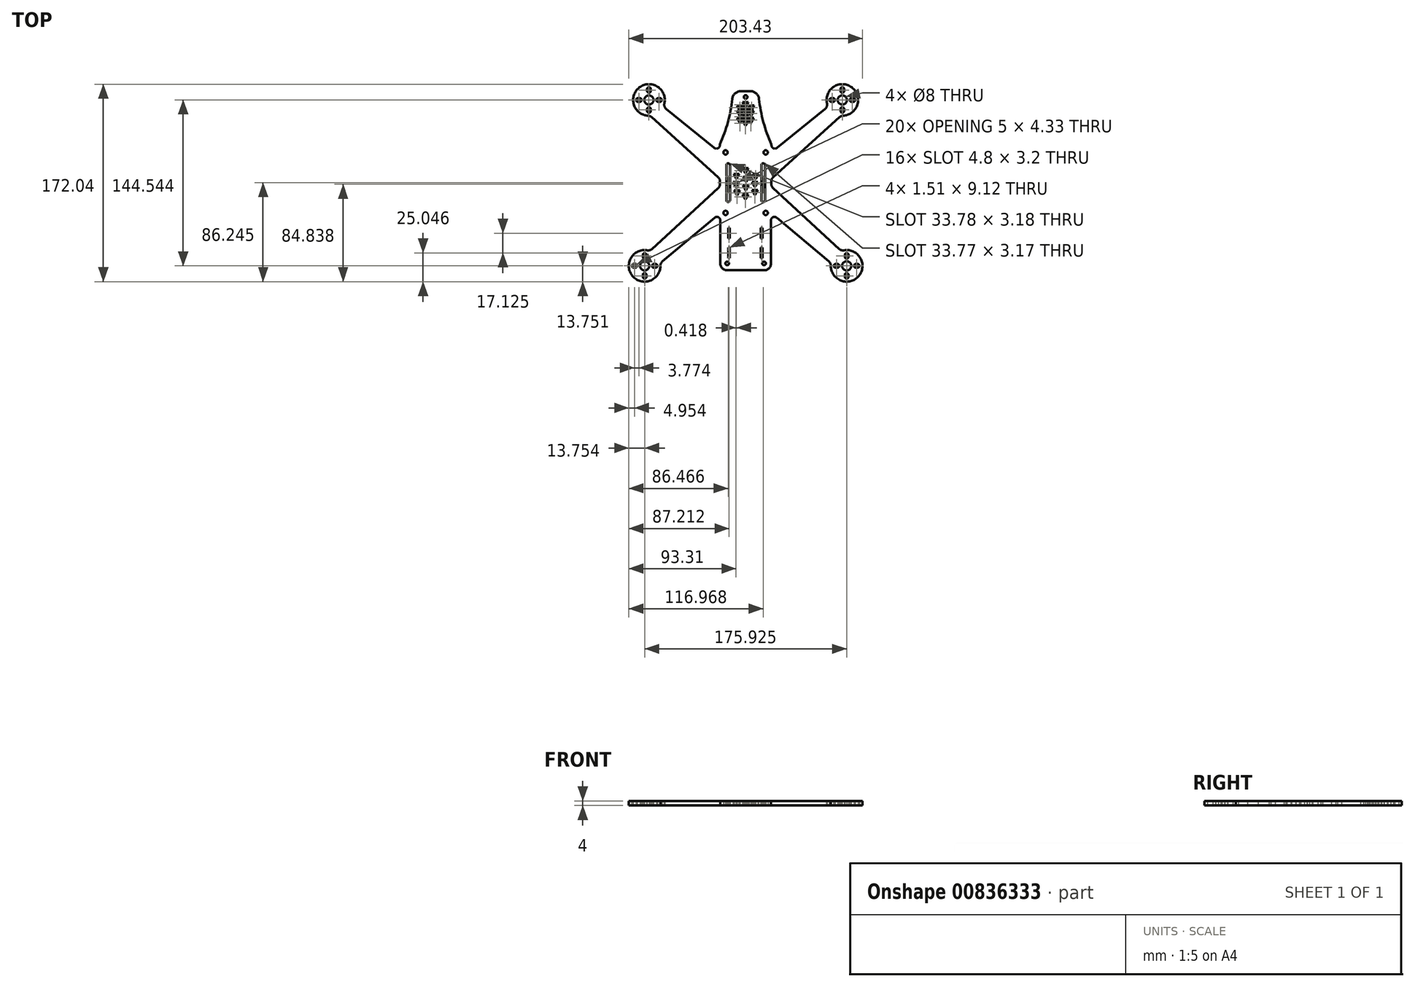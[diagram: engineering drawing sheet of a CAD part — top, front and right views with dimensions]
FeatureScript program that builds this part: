
annotation { "Feature Type Name" : "Feature", "Feature Type Description" : "" }
export const myFeature = defineFeature(function(context is Context, id is Id, definition is map)
    precondition{}
    {
        {
            var Q0;
            Q0=qCreatedBy(makeId("Top.planeOp"),FACE);
            var sketch = newSketch(context, id + "F0", { "sketchPlane" : qUnion([Q0])});
            skLineSegment(sketch, "E0.MirrorCS", {"start": v(-18.92, -69.92) * mm, "end": v(38.48, -122.77) * mm});
            skLineSegment(sketch, "E1.MirrorCS", {"start": v(-15.91, -95.57) * mm, "end": v(29.51, -133.68) * mm});
            skLineSegment(sketch, "E2.trimOffspring", {"start": v(-20.53, -63.92) * mm, "end": v(-20.53, -66.23) * mm});
            skLineSegment(sketch, "E3.MirrorCS", {"start": v(-18.88, -60.23) * mm, "end": v(38.94, -8.04) * mm});
            skLineSegment(sketch, "E4.MirrorCS", {"start": v(-15.53, -34.75) * mm, "end": v(26.13, -1.02) * mm});
            skArc(sketch, "E5.MirrorCS", {"start": v(-38.56, 7.2) * mm, "mid": v(-38.56, 7.2) * mm, "end": v(-38.56, 7.2) * mm});
            skLineSegment(sketch, "E6", {"start": v(-42.91, 14.57) * mm, "end": v(-38.56, 14.57) * mm});
            skLineSegment(sketch, "E7", {"start": v(-20.41, -31.7) * mm, "end": v(-20.41, -38.7) * mm});
            skLineSegment(sketch, "E8", {"start": v(-20.41, -32.42) * mm, "end": v(-20.41, -31.7) * mm});
            skArc(sketch, "E9", {"start": v(-31.23, 7.96) * mm, "mid": v(-27.44, -12.31) * mm, "end": v(-20.41, -31.7) * mm});
            skArc(sketch, "E10.filletArc", {"start": v(-31.23, 7.96) * mm, "mid": v(-33.63, 12.68) * mm, "end": v(-38.56, 14.57) * mm});
            skPoint(sketch, "E11.start.orphan", {"position": v(-47.26, 14.57) * mm});
            skLineSegment(sketch, "E12.MirrorCS", {"start": v(-42.91, 14.57) * mm, "end": v(-47.26, 14.57) * mm});
            skPoint(sketch, "E13.MirrorP", {"position": v(-47.26, 7.2) * mm});
            skPoint(sketch, "E14.MirrorP", {"position": v(-38.56, 14.57) * mm});
            skCircle(sketch, "E15", {"center": v(-42.91, 9.57) * mm, "radius": 1.59 * mm});
            skArc(sketch, "E16", {"start": v(31.3, -137.53) * mm, "mid": v(55.55, -146.44) * mm, "end": v(42.72, -124.02) * mm});
            skArc(sketch, "E17", {"start": v(42.02, -6.75) * mm, "mid": v(49.57, 17.94) * mm, "end": v(27.86, 3.96) * mm});
            skLineSegment(sketch, "E18.MirrorCS", {"start": v(33.27, 8.58) * mm, "end": v(31.67, 8.58) * mm});
            skArc(sketch, "E19.MirrorCS", {"start": v(33.27, 8.58) * mm, "mid": v(34.87, 6.98) * mm, "end": v(33.27, 5.38) * mm});
            skArc(sketch, "E20.MirrorCS", {"start": v(31.67, 5.38) * mm, "mid": v(30.07, 6.98) * mm, "end": v(31.67, 8.58) * mm});
            skArc(sketch, "E21.MirrorCS", {"start": v(42.87, 14.88) * mm, "mid": v(41.27, 13.28) * mm, "end": v(39.67, 14.88) * mm});
            skLineSegment(sketch, "E22.MirrorCS", {"start": v(42.87, 16.48) * mm, "end": v(42.87, 14.88) * mm});
            skLineSegment(sketch, "E23.MirrorCS", {"start": v(39.67, 16.48) * mm, "end": v(39.67, 14.88) * mm});
            skArc(sketch, "E24.MirrorCS", {"start": v(39.67, 16.48) * mm, "mid": v(41.27, 18.08) * mm, "end": v(42.87, 16.48) * mm});
            skLineSegment(sketch, "E25.MirrorCS", {"start": v(33.27, 5.38) * mm, "end": v(31.67, 5.38) * mm});
            skArc(sketch, "E26.MirrorCS", {"start": v(39.67, -0.92) * mm, "mid": v(41.27, 0.68) * mm, "end": v(42.87, -0.92) * mm});
            skLineSegment(sketch, "E27.MirrorCS", {"start": v(39.67, -2.52) * mm, "end": v(39.67, -0.92) * mm});
            skArc(sketch, "E28.MirrorCS", {"start": v(42.87, -2.52) * mm, "mid": v(41.27, -4.12) * mm, "end": v(39.67, -2.52) * mm});
            skLineSegment(sketch, "E29.MirrorCS", {"start": v(42.87, -0.92) * mm, "end": v(42.87, -2.52) * mm});
            skCircle(sketch, "E30.MirrorC", {"center": v(41.27, 6.98) * mm, "radius": 4 * mm});
            skLineSegment(sketch, "E31.MirrorCS", {"start": v(50.87, 8.58) * mm, "end": v(49.27, 8.58) * mm});
            skArc(sketch, "E32.MirrorCS", {"start": v(49.27, 5.38) * mm, "mid": v(47.67, 6.98) * mm, "end": v(49.27, 8.58) * mm});
            skLineSegment(sketch, "E33.MirrorCS", {"start": v(49.27, 5.38) * mm, "end": v(50.87, 5.38) * mm});
            skArc(sketch, "E34.MirrorCS", {"start": v(50.87, 8.58) * mm, "mid": v(52.47, 6.98) * mm, "end": v(50.87, 5.38) * mm});
            skLineSegment(sketch, "E35.MirrorCS", {"start": v(37.05, -135.97) * mm, "end": v(35.45, -135.97) * mm});
            skArc(sketch, "E36.MirrorCS", {"start": v(37.05, -135.97) * mm, "mid": v(38.65, -137.57) * mm, "end": v(37.05, -139.17) * mm});
            skArc(sketch, "E37.MirrorCS", {"start": v(35.45, -139.17) * mm, "mid": v(33.85, -137.57) * mm, "end": v(35.45, -135.97) * mm});
            skArc(sketch, "E38.MirrorCS", {"start": v(46.65, -129.67) * mm, "mid": v(45.05, -131.27) * mm, "end": v(43.45, -129.67) * mm});
            skLineSegment(sketch, "E39.MirrorCS", {"start": v(46.65, -128.07) * mm, "end": v(46.65, -129.67) * mm});
            skLineSegment(sketch, "E40.MirrorCS", {"start": v(43.45, -128.07) * mm, "end": v(43.45, -129.67) * mm});
            skArc(sketch, "E41.MirrorCS", {"start": v(43.45, -128.07) * mm, "mid": v(45.05, -126.47) * mm, "end": v(46.65, -128.07) * mm});
            skLineSegment(sketch, "E42.MirrorCS", {"start": v(37.05, -139.17) * mm, "end": v(35.45, -139.17) * mm});
            skArc(sketch, "E43.MirrorCS", {"start": v(43.45, -145.47) * mm, "mid": v(45.05, -143.87) * mm, "end": v(46.65, -145.47) * mm});
            skLineSegment(sketch, "E44.MirrorCS", {"start": v(43.45, -147.07) * mm, "end": v(43.45, -145.47) * mm});
            skArc(sketch, "E45.MirrorCS", {"start": v(46.65, -147.07) * mm, "mid": v(45.05, -148.67) * mm, "end": v(43.45, -147.07) * mm});
            skLineSegment(sketch, "E46.MirrorCS", {"start": v(46.65, -145.47) * mm, "end": v(46.65, -147.07) * mm});
            skCircle(sketch, "E47.MirrorC", {"center": v(45.05, -137.57) * mm, "radius": 4 * mm});
            skLineSegment(sketch, "E48.MirrorCS", {"start": v(54.65, -135.97) * mm, "end": v(53.05, -135.97) * mm});
            skArc(sketch, "E49.MirrorCS", {"start": v(53.05, -139.17) * mm, "mid": v(51.45, -137.57) * mm, "end": v(53.05, -135.97) * mm});
            skLineSegment(sketch, "E50.MirrorCS", {"start": v(53.05, -139.17) * mm, "end": v(54.65, -139.17) * mm});
            skArc(sketch, "E51.MirrorCS", {"start": v(54.65, -135.97) * mm, "mid": v(56.25, -137.57) * mm, "end": v(54.65, -139.17) * mm});
            skPoint(sketch, "E52.visualSharp", {"position": v(28.82, 1.16) * mm});
            skArc(sketch, "E52.filletArc", {"start": v(26.13, -1.02) * mm, "mid": v(27.7, 1.22) * mm, "end": v(27.86, 3.96) * mm});
            skPoint(sketch, "E53.visualSharp", {"position": v(40.37, -6.75) * mm});
            skArc(sketch, "E53.filletArc", {"start": v(42.02, -6.75) * mm, "mid": v(40.37, -7.13) * mm, "end": v(38.94, -8.04) * mm});
            skPoint(sketch, "E54.visualSharp", {"position": v(-20.52, -61.7) * mm});
            skArc(sketch, "E54.filletArc", {"start": v(-18.88, -60.23) * mm, "mid": v(-20.1, -61.9) * mm, "end": v(-20.53, -63.92) * mm});
            skPoint(sketch, "E55.visualSharp", {"position": v(-20.54, -68.43) * mm});
            skArc(sketch, "E55.filletArc", {"start": v(-20.53, -66.23) * mm, "mid": v(-20.12, -68.25) * mm, "end": v(-18.92, -69.92) * mm});
            skPoint(sketch, "E56.visualSharp", {"position": v(40.47, -124.6) * mm});
            skArc(sketch, "E56.filletArc", {"start": v(38.48, -122.77) * mm, "mid": v(40.45, -123.89) * mm, "end": v(42.72, -124.02) * mm});
            skPoint(sketch, "E57.visualSharp", {"position": v(31.48, -135.33) * mm});
            skArc(sketch, "E57.filletArc", {"start": v(31.3, -137.53) * mm, "mid": v(30.83, -135.4) * mm, "end": v(29.51, -133.68) * mm});
            skLineSegment(sketch, "E58.MirrorCS", {"start": v(-129.28, -128.07) * mm, "end": v(-129.28, -129.67) * mm});
            skLineSegment(sketch, "E59.MirrorCS", {"start": v(-119.1, 5.38) * mm, "end": v(-117.5, 5.38) * mm});
            skLineSegment(sketch, "E60.MirrorCS", {"start": v(-119.1, 8.58) * mm, "end": v(-117.5, 8.58) * mm});
            skArc(sketch, "E61.MirrorCS", {"start": v(-129.28, -128.07) * mm, "mid": v(-130.88, -126.47) * mm, "end": v(-132.48, -128.07) * mm});
            skLineSegment(sketch, "E62.MirrorCS", {"start": v(-136.7, 8.58) * mm, "end": v(-135.1, 8.58) * mm});
            skArc(sketch, "E63.MirrorCS", {"start": v(-119.1, 8.58) * mm, "mid": v(-120.7, 6.98) * mm, "end": v(-119.1, 5.38) * mm});
            skLineSegment(sketch, "E64.MirrorCS", {"start": v(-129.28, -147.07) * mm, "end": v(-129.28, -145.47) * mm});
            skLineSegment(sketch, "E65.MirrorCS", {"start": v(-135.1, 5.38) * mm, "end": v(-136.7, 5.38) * mm});
            skArc(sketch, "E66.MirrorCS", {"start": v(-132.48, -129.67) * mm, "mid": v(-130.88, -131.27) * mm, "end": v(-129.28, -129.67) * mm});
            skLineSegment(sketch, "E67.MirrorCS", {"start": v(-132.48, -128.07) * mm, "end": v(-132.48, -129.67) * mm});
            skArc(sketch, "E68.MirrorCS", {"start": v(-124.3, -122.77) * mm, "mid": v(-126.28, -123.89) * mm, "end": v(-128.54, -124.02) * mm});
            skLineSegment(sketch, "E69.MirrorCS", {"start": v(-132.48, -145.47) * mm, "end": v(-132.48, -147.07) * mm});
            skArc(sketch, "E70.MirrorCS", {"start": v(-117.5, 5.38) * mm, "mid": v(-115.9, 6.98) * mm, "end": v(-117.5, 8.58) * mm});
            skLineSegment(sketch, "E71.MirrorCS", {"start": v(-122.88, -135.97) * mm, "end": v(-121.28, -135.97) * mm});
            skArc(sketch, "E72.MirrorCS", {"start": v(-135.1, 5.38) * mm, "mid": v(-133.5, 6.98) * mm, "end": v(-135.1, 8.58) * mm});
            skArc(sketch, "E73.MirrorCS", {"start": v(-136.7, 8.58) * mm, "mid": v(-138.3, 6.98) * mm, "end": v(-136.7, 5.38) * mm});
            skLineSegment(sketch, "E74.MirrorCS", {"start": v(-128.7, -0.92) * mm, "end": v(-128.7, -2.52) * mm});
            skArc(sketch, "E75.MirrorCS", {"start": v(-132.48, -147.07) * mm, "mid": v(-130.88, -148.67) * mm, "end": v(-129.28, -147.07) * mm});
            skLineSegment(sketch, "E76.MirrorCS", {"start": v(-125.5, -2.52) * mm, "end": v(-125.5, -0.92) * mm});
            skArc(sketch, "E77.MirrorCS", {"start": v(-129.28, -145.47) * mm, "mid": v(-130.88, -143.87) * mm, "end": v(-132.48, -145.47) * mm});
            skArc(sketch, "E78.MirrorCS", {"start": v(-125.5, -0.92) * mm, "mid": v(-127.1, 0.68) * mm, "end": v(-128.7, -0.92) * mm});
            skArc(sketch, "E79.MirrorCS", {"start": v(-117.13, -137.53) * mm, "mid": v(-116.66, -135.4) * mm, "end": v(-115.34, -133.68) * mm});
            skArc(sketch, "E80.MirrorCS", {"start": v(-121.28, -139.17) * mm, "mid": v(-119.68, -137.57) * mm, "end": v(-121.28, -135.97) * mm});
            skLineSegment(sketch, "E81.MirrorCS", {"start": v(-122.88, -139.17) * mm, "end": v(-121.28, -139.17) * mm});
            skLineSegment(sketch, "E82.MirrorCS", {"start": v(-125.5, 16.48) * mm, "end": v(-125.5, 14.88) * mm});
            skArc(sketch, "E83.MirrorCS", {"start": v(-47.26, 7.2) * mm, "mid": v(-47.26, 7.2) * mm, "end": v(-47.26, 7.2) * mm});
            skLineSegment(sketch, "E84.MirrorCS", {"start": v(-128.7, 16.48) * mm, "end": v(-128.7, 14.88) * mm});
            skArc(sketch, "E85.MirrorCS", {"start": v(-128.7, -2.52) * mm, "mid": v(-127.1, -4.12) * mm, "end": v(-125.5, -2.52) * mm});
            skLineSegment(sketch, "E86.MirrorCS", {"start": v(-140.48, -135.97) * mm, "end": v(-138.88, -135.97) * mm});
            skArc(sketch, "E87.MirrorCS", {"start": v(-122.88, -135.97) * mm, "mid": v(-124.48, -137.57) * mm, "end": v(-122.88, -139.17) * mm});
            skArc(sketch, "E88.MirrorCS", {"start": v(-127.85, -6.75) * mm, "mid": v(-126.2, -7.13) * mm, "end": v(-124.77, -8.04) * mm});
            skArc(sketch, "E89.MirrorCS", {"start": v(-138.88, -139.17) * mm, "mid": v(-137.28, -137.57) * mm, "end": v(-138.88, -135.97) * mm});
            skArc(sketch, "E90.MirrorCS", {"start": v(-128.7, 14.88) * mm, "mid": v(-127.1, 13.28) * mm, "end": v(-125.5, 14.88) * mm});
            skCircle(sketch, "E91.MirrorC", {"center": v(-130.88, -137.57) * mm, "radius": 4 * mm});
            skArc(sketch, "E92.MirrorCS", {"start": v(-125.5, 16.48) * mm, "mid": v(-127.1, 18.08) * mm, "end": v(-128.7, 16.48) * mm});
            skCircle(sketch, "E93.MirrorC", {"center": v(-127.1, 6.98) * mm, "radius": 4 * mm});
            skArc(sketch, "E94.MirrorCS", {"start": v(-140.48, -135.97) * mm, "mid": v(-142.08, -137.57) * mm, "end": v(-140.48, -139.17) * mm});
            skLineSegment(sketch, "E95.MirrorCS", {"start": v(-138.88, -139.17) * mm, "end": v(-140.48, -139.17) * mm});
            skArc(sketch, "E96.MirrorCS", {"start": v(-111.95, -1.02) * mm, "mid": v(-113.53, 1.22) * mm, "end": v(-113.69, 3.96) * mm});
            skLineSegment(sketch, "E97.MirrorCS", {"start": v(-65.41, -32.42) * mm, "end": v(-65.41, -31.7) * mm});
            skLineSegment(sketch, "E98.MirrorCS", {"start": v(-65.3, -63.92) * mm, "end": v(-65.3, -66.23) * mm});
            skArc(sketch, "E99.MirrorCS", {"start": v(-66.95, -60.23) * mm, "mid": v(-65.74, -61.9) * mm, "end": v(-65.3, -63.92) * mm});
            skArc(sketch, "E100.MirrorCS", {"start": v(-65.3, -66.23) * mm, "mid": v(-65.71, -68.25) * mm, "end": v(-66.9, -69.92) * mm});
            skArc(sketch, "E101.MirrorCS", {"start": v(-54.6, 7.96) * mm, "mid": v(-52.2, 12.68) * mm, "end": v(-47.26, 14.57) * mm});
            skPoint(sketch, "E102.MirrorP", {"position": v(-126.3, -124.6) * mm});
            skLineSegment(sketch, "E103.MirrorCS", {"start": v(-70.3, -34.75) * mm, "end": v(-111.95, -1.02) * mm});
            skArc(sketch, "E104.MirrorCS", {"start": v(-54.6, 7.96) * mm, "mid": v(-58.39, -12.31) * mm, "end": v(-65.41, -31.7) * mm});
            skPoint(sketch, "E105.MirrorP", {"position": v(-65.3, -61.7) * mm});
            skPoint(sketch, "E106.MirrorP", {"position": v(-114.64, 1.16) * mm});
            skPoint(sketch, "E107.MirrorP", {"position": v(-117.3, -135.33) * mm});
            skPoint(sketch, "E108.MirrorP", {"position": v(-65.28, -68.43) * mm});
            skLineSegment(sketch, "E109.MirrorCS", {"start": v(-66.95, -60.23) * mm, "end": v(-124.77, -8.04) * mm});
            skArc(sketch, "E110.MirrorCS", {"start": v(-117.13, -137.53) * mm, "mid": v(-141.38, -146.44) * mm, "end": v(-128.54, -124.02) * mm});
            skArc(sketch, "E111.MirrorCS", {"start": v(-127.85, -6.75) * mm, "mid": v(-135.4, 17.94) * mm, "end": v(-113.69, 3.96) * mm});
            skLineSegment(sketch, "E112.MirrorCS", {"start": v(-69.92, -95.57) * mm, "end": v(-115.34, -133.68) * mm});
            skPoint(sketch, "E113.MirrorP", {"position": v(-126.2, -6.75) * mm});
            skLineSegment(sketch, "E114.MirrorCS", {"start": v(-66.9, -69.92) * mm, "end": v(-124.3, -122.77) * mm});
            skLineSegment(sketch, "E115", {"start": v(-64.99, -97.87) * mm, "end": v(-64.99, -135.43) * mm});
            skLineSegment(sketch, "E116", {"start": v(-58.99, -141.43) * mm, "end": v(-26.84, -141.43) * mm});
            skLineSegment(sketch, "E117", {"start": v(-20.84, -97.87) * mm, "end": v(-20.84, -135.43) * mm});
            skPoint(sketch, "E118.visualSharp", {"position": v(-64.99, -141.43) * mm});
            skArc(sketch, "E118.filletArc", {"start": v(-64.99, -135.43) * mm, "mid": v(-63.23, -139.67) * mm, "end": v(-58.99, -141.43) * mm});
            skPoint(sketch, "E119.visualSharp", {"position": v(-20.84, -141.43) * mm});
            skArc(sketch, "E119.filletArc", {"start": v(-26.84, -141.43) * mm, "mid": v(-22.6, -139.67) * mm, "end": v(-20.84, -135.43) * mm});
            skCircle(sketch, "E120", {"center": v(-26.84, -135.43) * mm, "radius": 1.59 * mm});
            skCircle(sketch, "E121", {"center": v(-58.99, -135.43) * mm, "radius": 1.59 * mm});
            skLineSegment(sketch, "E122.0", {"start": v(-40.36, -0.31) * mm, "end": v(-42.86, -4.64) * mm});
            skLineSegment(sketch, "E122.1", {"start": v(-42.86, -4.64) * mm, "end": v(-45.36, -0.31) * mm});
            skLineSegment(sketch, "E122.2", {"start": v(-45.36, -0.31) * mm, "end": v(-40.36, -0.31) * mm});
            skPoint(sketch, "E122.0.midPoint", {"position": v(-41.61, -2.48) * mm});
            skLineSegment(sketch, "E123.0", {"start": v(-45.33, -2.7) * mm, "end": v(-47.83, -7.03) * mm});
            skLineSegment(sketch, "E123.1", {"start": v(-47.83, -7.03) * mm, "end": v(-50.33, -2.7) * mm});
            skLineSegment(sketch, "E123.2", {"start": v(-50.33, -2.7) * mm, "end": v(-45.33, -2.7) * mm});
            skPoint(sketch, "E123.0.midPoint", {"position": v(-46.58, -4.87) * mm});
            skLineSegment(sketch, "E124.0", {"start": v(-40.62, -5.4) * mm, "end": v(-43.12, -9.74) * mm});
            skLineSegment(sketch, "E124.1", {"start": v(-43.12, -9.74) * mm, "end": v(-45.62, -5.4) * mm});
            skLineSegment(sketch, "E124.2", {"start": v(-45.62, -5.4) * mm, "end": v(-40.62, -5.4) * mm});
            skPoint(sketch, "E124.0.midPoint", {"position": v(-41.87, -7.57) * mm});
            skLineSegment(sketch, "E125.0", {"start": v(-35.65, -2.7) * mm, "end": v(-38.15, -7.03) * mm});
            skLineSegment(sketch, "E125.1", {"start": v(-38.15, -7.03) * mm, "end": v(-40.65, -2.7) * mm});
            skLineSegment(sketch, "E125.2", {"start": v(-40.65, -2.7) * mm, "end": v(-35.65, -2.7) * mm});
            skPoint(sketch, "E125.0.midPoint", {"position": v(-36.9, -4.87) * mm});
            skLineSegment(sketch, "E126.0", {"start": v(-35.35, 2.37) * mm, "end": v(-37.85, -1.96) * mm});
            skLineSegment(sketch, "E126.1", {"start": v(-37.85, -1.96) * mm, "end": v(-40.35, 2.37) * mm});
            skLineSegment(sketch, "E126.2", {"start": v(-40.35, 2.37) * mm, "end": v(-35.35, 2.37) * mm});
            skPoint(sketch, "E126.0.midPoint", {"position": v(-36.6, 0.2) * mm});
            skLineSegment(sketch, "E127.0", {"start": v(-40.47, 4.97) * mm, "end": v(-42.97, 0.64) * mm});
            skLineSegment(sketch, "E127.1", {"start": v(-42.97, 0.64) * mm, "end": v(-45.47, 4.97) * mm});
            skLineSegment(sketch, "E127.2", {"start": v(-45.47, 4.97) * mm, "end": v(-40.47, 4.97) * mm});
            skPoint(sketch, "E127.0.midPoint", {"position": v(-41.72, 2.8) * mm});
            skLineSegment(sketch, "E128.0", {"start": v(-45.25, 2.37) * mm, "end": v(-47.75, -1.96) * mm});
            skLineSegment(sketch, "E128.1", {"start": v(-47.75, -1.96) * mm, "end": v(-50.25, 2.37) * mm});
            skLineSegment(sketch, "E128.2", {"start": v(-50.25, 2.37) * mm, "end": v(-45.25, 2.37) * mm});
            skPoint(sketch, "E128.0.midPoint", {"position": v(-46.5, 0.2) * mm});
            skLineSegment(sketch, "E129.0", {"start": v(-35.89, -8.43) * mm, "end": v(-38.39, -12.77) * mm});
            skLineSegment(sketch, "E129.1", {"start": v(-38.39, -12.77) * mm, "end": v(-40.89, -8.43) * mm});
            skLineSegment(sketch, "E129.2", {"start": v(-40.89, -8.43) * mm, "end": v(-35.89, -8.43) * mm});
            skPoint(sketch, "E129.0.midPoint", {"position": v(-37.14, -10.6) * mm});
            skLineSegment(sketch, "E130.0", {"start": v(-45.25, -8.43) * mm, "end": v(-47.75, -12.77) * mm});
            skLineSegment(sketch, "E130.1", {"start": v(-47.75, -12.77) * mm, "end": v(-50.25, -8.43) * mm});
            skLineSegment(sketch, "E130.2", {"start": v(-50.25, -8.43) * mm, "end": v(-45.25, -8.43) * mm});
            skPoint(sketch, "E130.0.midPoint", {"position": v(-46.5, -10.6) * mm});
            skLineSegment(sketch, "E131.0", {"start": v(-40.47, -11.03) * mm, "end": v(-42.97, -15.36) * mm});
            skLineSegment(sketch, "E131.1", {"start": v(-42.97, -15.36) * mm, "end": v(-45.47, -11.03) * mm});
            skLineSegment(sketch, "E131.2", {"start": v(-45.47, -11.03) * mm, "end": v(-40.47, -11.03) * mm});
            skPoint(sketch, "E131.0.midPoint", {"position": v(-41.72, -13.2) * mm});
            skLineSegment(sketch, "E132.bottom", {"start": v(-58.17, -121.71) * mm, "end": v(-56.66, -121.71) * mm});
            skLineSegment(sketch, "E132.top", {"start": v(-58.17, -130.84) * mm, "end": v(-56.66, -130.84) * mm});
            skLineSegment(sketch, "E132.left", {"start": v(-58.17, -121.71) * mm, "end": v(-58.17, -130.84) * mm});
            skLineSegment(sketch, "E132.right", {"start": v(-56.66, -121.71) * mm, "end": v(-56.66, -130.84) * mm});
            skLineSegment(sketch, "E133.MirrorCS", {"start": v(-28.14, -121.71) * mm, "end": v(-28.14, -130.84) * mm});
            skLineSegment(sketch, "E134.MirrorCS", {"start": v(-29.65, -121.71) * mm, "end": v(-29.65, -130.84) * mm});
            skLineSegment(sketch, "E135.MirrorCS", {"start": v(-28.14, -121.71) * mm, "end": v(-29.65, -121.71) * mm});
            skLineSegment(sketch, "E136.MirrorCS", {"start": v(-28.14, -130.84) * mm, "end": v(-29.65, -130.84) * mm});
            skPoint(sketch, "E137.visualSharp", {"position": v(-20.84, -91.43) * mm});
            skArc(sketch, "E137.filletArc", {"start": v(-15.91, -95.57) * mm, "mid": v(-19.1, -95.15) * mm, "end": v(-20.84, -97.87) * mm});
            skPoint(sketch, "E138.visualSharp", {"position": v(-64.99, -91.43) * mm});
            skArc(sketch, "E138.filletArc", {"start": v(-64.99, -97.87) * mm, "mid": v(-66.72, -95.15) * mm, "end": v(-69.92, -95.57) * mm});
            skPoint(sketch, "E139.visualSharp", {"position": v(-65.41, -38.7) * mm});
            skArc(sketch, "E139.filletArc", {"start": v(-70.3, -34.75) * mm, "mid": v(-67.12, -35.13) * mm, "end": v(-65.41, -32.42) * mm});
            skPoint(sketch, "E140.visualSharp", {"position": v(-20.41, -38.7) * mm});
            skArc(sketch, "E140.filletArc", {"start": v(-20.41, -32.42) * mm, "mid": v(-18.7, -35.13) * mm, "end": v(-15.53, -34.75) * mm});
            skPoint(sketch, "E141.startSnap0", {"position": v(-65.3, -65.08) * mm});
            skArc(sketch, "E142", {"start": v(-26.08, -49.89) * mm, "mid": v(-27.66, -48.19) * mm, "end": v(-29.25, -49.9) * mm});
            skLineSegment(sketch, "E143", {"start": v(-58.16, -49.78) * mm, "end": v(-58.16, -49.78) * mm});
            skArc(sketch, "E144", {"start": v(-56.58, -49.78) * mm, "mid": v(-58.16, -48.19) * mm, "end": v(-59.75, -49.78) * mm});
            skArc(sketch, "E145.MirrorC", {"start": v(-56.58, -80.38) * mm, "mid": v(-58.16, -81.96) * mm, "end": v(-59.75, -80.38) * mm});
            skArc(sketch, "E146.MirrorC", {"start": v(-26.08, -80.38) * mm, "mid": v(-27.72, -81.96) * mm, "end": v(-29.25, -80.26) * mm});
            skLineSegment(sketch, "E147", {"start": v(-59.75, -49.78) * mm, "end": v(-59.75, -80.38) * mm});
            skLineSegment(sketch, "E148", {"start": v(-56.58, -49.78) * mm, "end": v(-56.58, -80.38) * mm});
            skLineSegment(sketch, "E149", {"start": v(-29.25, -49.66) * mm, "end": v(-29.25, -80.38) * mm});
            skLineSegment(sketch, "E150", {"start": v(-26.08, -49.66) * mm, "end": v(-26.08, -80.38) * mm});
            skPoint(sketch, "E151.orphan", {"position": v(-58.16, -65.08) * mm});
            skCircle(sketch, "E152", {"center": v(-60.41, -38.7) * mm, "radius": 1.88 * mm});
            skCircle(sketch, "E153.MirrorC", {"center": v(-25.41, -38.7) * mm, "radius": 1.88 * mm});
            skLineSegment(sketch, "E154.MirrorCS", {"start": v(-28.14, -104.59) * mm, "end": v(-29.65, -104.59) * mm});
            skLineSegment(sketch, "E155.MirrorCS", {"start": v(-58.17, -113.71) * mm, "end": v(-56.66, -113.71) * mm});
            skLineSegment(sketch, "E156.MirrorCS", {"start": v(-28.14, -113.71) * mm, "end": v(-29.65, -113.71) * mm});
            skLineSegment(sketch, "E157.MirrorCS", {"start": v(-58.17, -104.59) * mm, "end": v(-56.66, -104.59) * mm});
            skLineSegment(sketch, "E158.MirrorCS", {"start": v(-58.17, -113.71) * mm, "end": v(-58.17, -104.59) * mm});
            skLineSegment(sketch, "E159.MirrorCS", {"start": v(-28.14, -113.71) * mm, "end": v(-28.14, -104.59) * mm});
            skLineSegment(sketch, "E160.MirrorCS", {"start": v(-29.65, -113.71) * mm, "end": v(-29.65, -104.59) * mm});
            skLineSegment(sketch, "E161.MirrorCS", {"start": v(-56.66, -113.71) * mm, "end": v(-56.66, -104.59) * mm});
            skCircle(sketch, "E162.MirrorC", {"center": v(-60.41, -91.44) * mm, "radius": 1.88 * mm});
            skCircle(sketch, "E163.MirrorC", {"center": v(-25.41, -91.44) * mm, "radius": 1.88 * mm});
            skLineSegment(sketch, "E164", {"start": v(-58.16, -49.78) * mm, "end": v(-58.16, -80.38) * mm});
            skLineSegment(sketch, "E165", {"start": v(-27.66, -49.78) * mm, "end": v(-27.66, -80.38) * mm});
            skPoint(sketch, "E166.endSnap0", {"position": v(-29.25, -65.02) * mm});
            skPoint(sketch, "E167", {"position": v(-42.91, -65.05) * mm});
            skLineSegment(sketch, "E168.0", {"start": v(-39.96, -59.89) * mm, "end": v(-42.46, -64.22) * mm});
            skLineSegment(sketch, "E168.1", {"start": v(-42.46, -64.22) * mm, "end": v(-44.96, -59.89) * mm});
            skLineSegment(sketch, "E168.2", {"start": v(-44.96, -59.89) * mm, "end": v(-39.96, -59.89) * mm});
            skPoint(sketch, "E168.0.midPoint", {"position": v(-41.21, -62.05) * mm});
            skLineSegment(sketch, "E169.0", {"start": v(-48.82, -64.32) * mm, "end": v(-51.32, -68.65) * mm});
            skLineSegment(sketch, "E169.1", {"start": v(-51.32, -68.65) * mm, "end": v(-53.82, -64.32) * mm});
            skLineSegment(sketch, "E169.2", {"start": v(-53.82, -64.32) * mm, "end": v(-48.82, -64.32) * mm});
            skPoint(sketch, "E169.0.midPoint", {"position": v(-50.07, -66.48) * mm});
            skLineSegment(sketch, "E170.0", {"start": v(-40.19, -67.35) * mm, "end": v(-42.69, -71.68) * mm});
            skLineSegment(sketch, "E170.1", {"start": v(-42.69, -71.68) * mm, "end": v(-45.19, -67.35) * mm});
            skLineSegment(sketch, "E170.2", {"start": v(-45.19, -67.35) * mm, "end": v(-40.19, -67.35) * mm});
            skPoint(sketch, "E170.0.midPoint", {"position": v(-41.44, -69.51) * mm});
            skLineSegment(sketch, "E171.0", {"start": v(-32.31, -64.32) * mm, "end": v(-34.81, -68.65) * mm});
            skLineSegment(sketch, "E171.1", {"start": v(-34.81, -68.65) * mm, "end": v(-37.31, -64.32) * mm});
            skLineSegment(sketch, "E171.2", {"start": v(-37.31, -64.32) * mm, "end": v(-32.31, -64.32) * mm});
            skPoint(sketch, "E171.0.midPoint", {"position": v(-33.56, -66.48) * mm});
            skLineSegment(sketch, "E172.0", {"start": v(-31.7, -57.45) * mm, "end": v(-34.2, -61.78) * mm});
            skLineSegment(sketch, "E172.1", {"start": v(-34.2, -61.78) * mm, "end": v(-36.7, -57.45) * mm});
            skLineSegment(sketch, "E172.2", {"start": v(-36.7, -57.45) * mm, "end": v(-31.7, -57.45) * mm});
            skPoint(sketch, "E172.0.midPoint", {"position": v(-32.96, -59.62) * mm});
            skLineSegment(sketch, "E173.0", {"start": v(-40.54, -52.54) * mm, "end": v(-43.04, -56.87) * mm});
            skLineSegment(sketch, "E173.1", {"start": v(-43.04, -56.87) * mm, "end": v(-45.54, -52.54) * mm});
            skLineSegment(sketch, "E173.2", {"start": v(-45.54, -52.54) * mm, "end": v(-40.54, -52.54) * mm});
            skPoint(sketch, "E173.0.midPoint", {"position": v(-41.8, -54.7) * mm});
            skLineSegment(sketch, "E174.0", {"start": v(-48.4, -57.5) * mm, "end": v(-50.9, -61.84) * mm});
            skLineSegment(sketch, "E174.1", {"start": v(-50.9, -61.84) * mm, "end": v(-53.4, -57.5) * mm});
            skLineSegment(sketch, "E174.2", {"start": v(-53.4, -57.5) * mm, "end": v(-48.4, -57.5) * mm});
            skPoint(sketch, "E174.0.midPoint", {"position": v(-49.65, -59.67) * mm});
            skLineSegment(sketch, "E175.0", {"start": v(-32.47, -71.48) * mm, "end": v(-34.97, -75.81) * mm});
            skLineSegment(sketch, "E175.1", {"start": v(-34.97, -75.81) * mm, "end": v(-37.47, -71.48) * mm});
            skLineSegment(sketch, "E175.2", {"start": v(-37.47, -71.48) * mm, "end": v(-32.47, -71.48) * mm});
            skPoint(sketch, "E175.0.midPoint", {"position": v(-33.72, -73.65) * mm});
            skLineSegment(sketch, "E176.0", {"start": v(-47.96, -71.74) * mm, "end": v(-50.46, -76.07) * mm});
            skLineSegment(sketch, "E176.1", {"start": v(-50.46, -76.07) * mm, "end": v(-52.96, -71.74) * mm});
            skLineSegment(sketch, "E176.2", {"start": v(-52.96, -71.74) * mm, "end": v(-47.96, -71.74) * mm});
            skPoint(sketch, "E176.0.midPoint", {"position": v(-49.21, -73.9) * mm});
            skLineSegment(sketch, "E177.0", {"start": v(-40.5, -75.17) * mm, "end": v(-43, -79.5) * mm});
            skLineSegment(sketch, "E177.1", {"start": v(-43, -79.5) * mm, "end": v(-45.5, -75.17) * mm});
            skLineSegment(sketch, "E177.2", {"start": v(-45.5, -75.17) * mm, "end": v(-40.5, -75.17) * mm});
            skPoint(sketch, "E177.0.midPoint", {"position": v(-41.74, -77.33) * mm});
            skSolve(sketch);
        }
        {
            var Q0;
            Q0=makeQuery(id+"F0.imprint","IMPRINT",FACE,{"disambiguationData":[TD([[makeQuery(id+"F0.imprint","IMPRINT",EDGE,{"derivedFrom":sQuery(id+"F0.wireOp",EDGE,"E0.MirrorCS")}),-1.0]])]});
            extrude(context, id + "F1", {"entities" : qUnion([Q0]), "depth" : 4 * mm, "offsetDistance" : 25 * mm});
        }
    });
